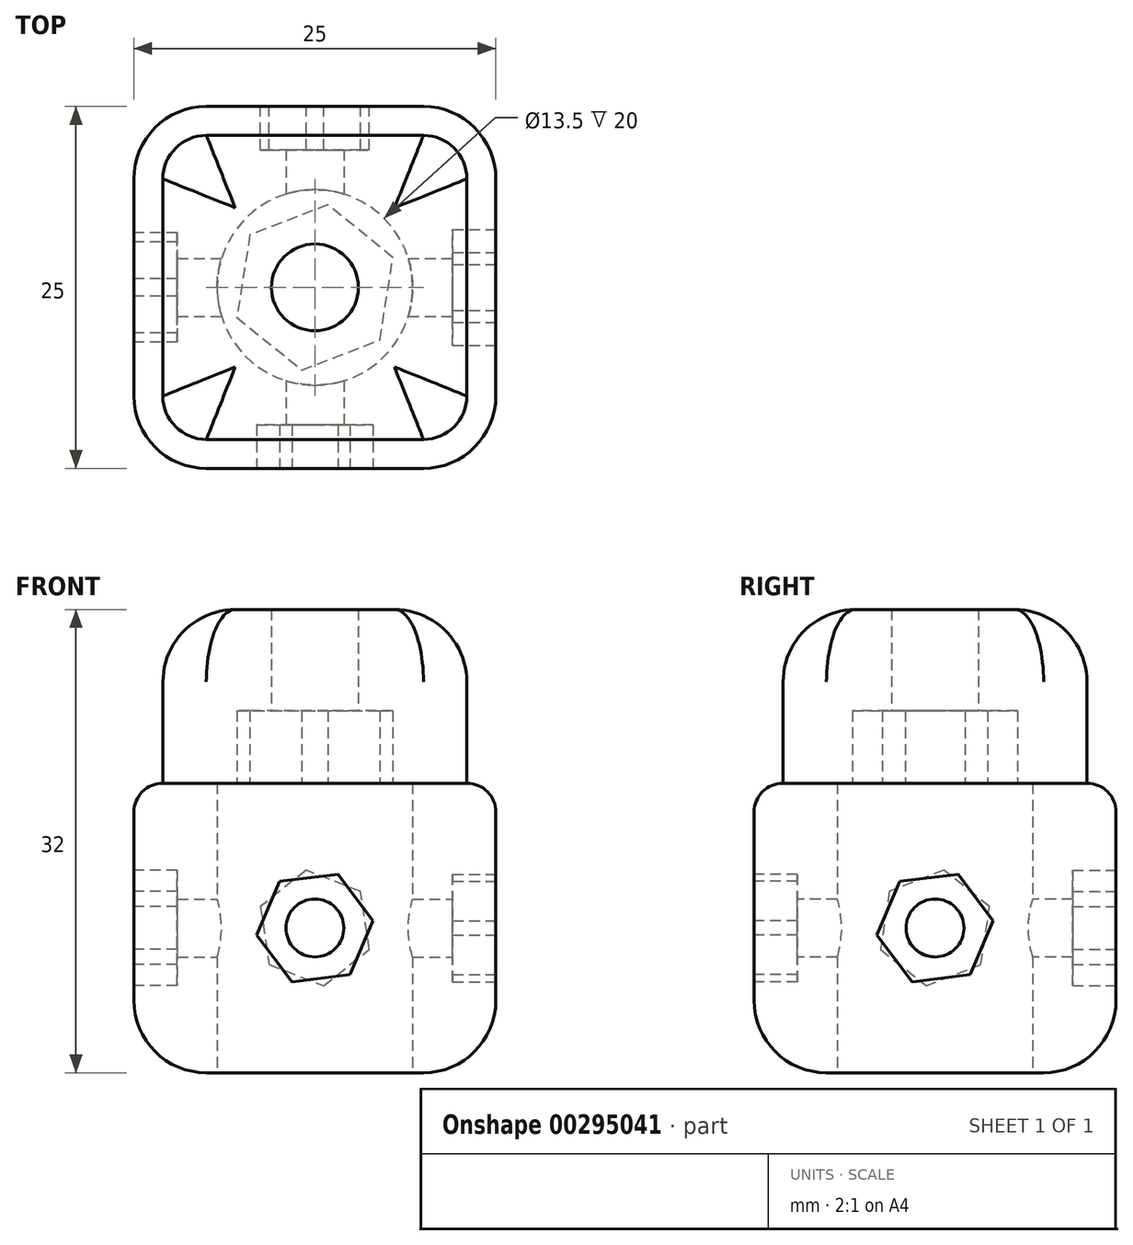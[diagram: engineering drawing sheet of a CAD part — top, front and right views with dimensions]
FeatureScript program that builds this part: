
annotation { "Feature Type Name" : "Feature", "Feature Type Description" : "" }
export const myFeature = defineFeature(function(context is Context, id is Id, definition is map)
    precondition{}
    {
        {
            var Q0;
            Q0=qCreatedBy(makeId("Top.planeOp"),FACE);
            var sketch = newSketch(context, id + "F0", { "sketchPlane" : qUnion([Q0])});
            skLineSegment(sketch, "E0.bottom", {"start": v(12.5, 12.5) * mm, "end": v(-12.5, 12.5) * mm});
            skLineSegment(sketch, "E0.top", {"start": v(12.5, -12.5) * mm, "end": v(-12.5, -12.5) * mm});
            skLineSegment(sketch, "E0.left", {"start": v(12.5, 12.5) * mm, "end": v(12.5, -12.5) * mm});
            skLineSegment(sketch, "E0.right", {"start": v(-12.5, 12.5) * mm, "end": v(-12.5, -12.5) * mm});
            skPoint(sketch, "E0.middle", {"position": v(0, 0) * mm});
            skSolve(sketch);
        }
        {
            var Q0;
            Q0 = qSketchRegion(id + "F0", true);
            extrude(context, id + "F1", {"entities" : qUnion([Q0]), "depth" : 20 * mm});
        }
        {
            var Q0;
            Q0=makeQuery(id+"F1.opExtrude","CAP_FACE",FACE,{"disambiguationData":[OSD([sQuery(id+"F0.wireOp",EDGE,"E0.bottom"),sQuery(id+"F0.wireOp",EDGE,"E0.top"),sQuery(id+"F0.wireOp",EDGE,"E0.left"),sQuery(id+"F0.wireOp",EDGE,"E0.right")])],"isStart":false});
            var sketch = newSketch(context, id + "F2", { "sketchPlane" : qUnion([Q0])});
            skLineSegment(sketch, "E1.bottom", {"start": v(10.5, 10.5) * mm, "end": v(-10.5, 10.5) * mm});
            skLineSegment(sketch, "E1.top", {"start": v(10.5, -10.5) * mm, "end": v(-10.5, -10.5) * mm});
            skLineSegment(sketch, "E1.left", {"start": v(10.5, 10.5) * mm, "end": v(10.5, -10.5) * mm});
            skLineSegment(sketch, "E1.right", {"start": v(-10.5, 10.5) * mm, "end": v(-10.5, -10.5) * mm});
            skSolve(sketch);
        }
        {
            var Q0;
            Q0=makeQuery(id+"F2.imprint","IMPRINT",FACE,{"disambiguationData":[TD([[makeQuery(id+"F2.imprint","IMPRINT",EDGE,{"derivedFrom":sQuery(id+"F2.wireOp",EDGE,"E1.bottom")}),1.0]])]});
            extrude(context, id + "F3", {"entities" : qUnion([Q0]), "operationType" : NewBodyOperationType.ADD, "depth" : 12 * mm});
        }
        {
            var Q0;
            Q0=makeQuery(id+"F1.opExtrude","CAP_FACE",FACE,{"disambiguationData":[OSD([sQuery(id+"F0.wireOp",EDGE,"E0.bottom"),sQuery(id+"F0.wireOp",EDGE,"E0.top"),sQuery(id+"F0.wireOp",EDGE,"E0.left"),sQuery(id+"F0.wireOp",EDGE,"E0.right")])],"isStart":true});
            var sketch = newSketch(context, id + "F4", { "sketchPlane" : qUnion([Q0])});
            skCircle(sketch, "E2", {"center": v(0, 0) * mm, "radius": 6.75 * mm});
            skSolve(sketch);
        }
        {
            var Q0;
            Q0=makeQuery(id+"F4.imprint","IMPRINT",FACE,{"disambiguationData":[TD([[makeQuery(id+"F4.imprint","IMPRINT",EDGE,{"derivedFrom":sQuery(id+"F4.wireOp",EDGE,"E2")}),1.0]])]});
            extrude(context, id + "F5", {"entities" : qUnion([Q0]), "operationType" : NewBodyOperationType.REMOVE, "oppositeDirection" : true, "depth" : 20 * mm});
        }
        {
            var Q0;
            Q0=makeQuery(id+"F1.opExtrude","CAP_FACE",FACE,{"disambiguationData":[OSD([sQuery(id+"F0.wireOp",EDGE,"E0.bottom"),sQuery(id+"F0.wireOp",EDGE,"E0.top"),sQuery(id+"F0.wireOp",EDGE,"E0.left"),sQuery(id+"F0.wireOp",EDGE,"E0.right")])],"isStart":true});
            var sketch = newSketch(context, id + "F6", { "sketchPlane" : qUnion([Q0])});
            skCircle(sketch, "E3", {"center": v(0, 0) * mm, "radius": 3 * mm});
            skSolve(sketch);
        }
        {
            var Q0;
            Q0 = qSketchRegion(id + "F6", true);
            extrude(context, id + "F7", {"entities" : qUnion([Q0]), "operationType" : NewBodyOperationType.REMOVE, "endBound" : BoundingType.THROUGH_ALL, "oppositeDirection" : true, "depth" : 25 * mm});
        }
        {
            var Q0;
            Q0=makeQuery(id+"F1.opExtrude","SWEPT_FACE",FACE,{"disambiguationData":[OSD([sQuery(id+"F0.wireOp",EDGE,"E0.right")])]});
            var sketch = newSketch(context, id + "F8", { "sketchPlane" : qUnion([Q0])});
            skLineSegment(sketch, "E4", {"start": v(-12.5, 0) * mm, "end": v(12.5, 20) * mm, "construction": true});
            skPoint(sketch, "E5.0.midPoint", {"position": v(1.27, 7.28) * mm});
            skCircle(sketch, "E6.cCircle", {"center": v(0, 10) * mm, "radius": 3.5 * mm, "construction": true});
            skLineSegment(sketch, "E6.0", {"start": v(3.76, 8.53) * mm, "end": v(0.6, 6) * mm});
            skLineSegment(sketch, "E6.1", {"start": v(0.6, 6) * mm, "end": v(-3.16, 7.48) * mm});
            skLineSegment(sketch, "E6.2", {"start": v(-3.16, 7.48) * mm, "end": v(-3.76, 11.47) * mm});
            skLineSegment(sketch, "E6.3", {"start": v(-3.76, 11.47) * mm, "end": v(-0.6, 14) * mm});
            skLineSegment(sketch, "E6.4", {"start": v(-0.6, 14) * mm, "end": v(3.16, 12.52) * mm});
            skLineSegment(sketch, "E6.5", {"start": v(3.16, 12.52) * mm, "end": v(3.76, 8.53) * mm});
            skPoint(sketch, "E6.0.midPoint", {"position": v(2.19, 7.27) * mm});
            skSolve(sketch);
        }
        {
            var Q0;
            Q0 = qSketchRegion(id + "F8", true);
            extrude(context, id + "F9", {"entities" : qUnion([Q0]), "operationType" : NewBodyOperationType.REMOVE, "oppositeDirection" : true, "depth" : 3 * mm});
        }
        {
            var Q0;
            Q0=makeQuery(id+"F1.opExtrude","SWEPT_FACE",FACE,{"disambiguationData":[OSD([sQuery(id+"F0.wireOp",EDGE,"E0.bottom")])]});
            var sketch = newSketch(context, id + "F10", { "sketchPlane" : qUnion([Q0])});
            skLineSegment(sketch, "E7", {"start": v(-12.5, 20) * mm, "end": v(12.5, 0) * mm, "construction": true});
            skCircle(sketch, "E8.cCircle", {"center": v(0, 10) * mm, "radius": 3.5 * mm, "construction": true});
            skLineSegment(sketch, "E8.0", {"start": v(-0.6, 6) * mm, "end": v(-3.76, 8.53) * mm});
            skLineSegment(sketch, "E8.1", {"start": v(-3.76, 8.53) * mm, "end": v(-3.16, 12.52) * mm});
            skLineSegment(sketch, "E8.2", {"start": v(-3.16, 12.52) * mm, "end": v(0.6, 14) * mm});
            skLineSegment(sketch, "E8.3", {"start": v(0.6, 14) * mm, "end": v(3.76, 11.47) * mm});
            skLineSegment(sketch, "E8.4", {"start": v(3.76, 11.47) * mm, "end": v(3.16, 7.48) * mm});
            skLineSegment(sketch, "E8.5", {"start": v(3.16, 7.48) * mm, "end": v(-0.6, 6) * mm});
            skPoint(sketch, "E8.0.midPoint", {"position": v(-2.19, 7.27) * mm});
            skSolve(sketch);
        }
        {
            var Q0;
            Q0=makeQuery(id+"F1.opExtrude","SWEPT_EDGE",EDGE,{"disambiguationData":[OSD([sQuery(id+"F0.wireOp",EDGE,"E0.bottom"),sQuery(id+"F0.wireOp",EDGE,"E0.left")])]});
            var Q1;
            Q1=makeQuery(id+"F1.opExtrude","SWEPT_EDGE",EDGE,{"disambiguationData":[OSD([sQuery(id+"F0.wireOp",EDGE,"E0.bottom"),sQuery(id+"F0.wireOp",EDGE,"E0.right")])]});
            var Q2;
            Q2=makeQuery(id+"F1.opExtrude","SWEPT_EDGE",EDGE,{"disambiguationData":[OSD([sQuery(id+"F0.wireOp",EDGE,"E0.top"),sQuery(id+"F0.wireOp",EDGE,"E0.left")])]});
            var Q3;
            Q3=makeQuery(id+"F1.opExtrude","SWEPT_EDGE",EDGE,{"disambiguationData":[OSD([sQuery(id+"F0.wireOp",EDGE,"E0.top"),sQuery(id+"F0.wireOp",EDGE,"E0.right")])]});
            fillet(context, id + "F11", {"entities" : qUnion([Q0, Q1, Q2, Q3]), "radius" : 5 * mm, "tangentPropagation" : true, "allowEdgeOverflow" : false});
        }
        {
            var Q0;
            Q0=makeQuery(id+"F3.opExtrude","SWEPT_EDGE",EDGE,{"disambiguationData":[OSD([sQuery(id+"F2.wireOp",EDGE,"E1.bottom"),sQuery(id+"F2.wireOp",EDGE,"E1.right")])]});
            var Q1;
            Q1=makeQuery(id+"F3.opExtrude","SWEPT_EDGE",EDGE,{"disambiguationData":[OSD([sQuery(id+"F2.wireOp",EDGE,"E1.top"),sQuery(id+"F2.wireOp",EDGE,"E1.right")])]});
            var Q2;
            Q2=makeQuery(id+"F3.opExtrude","SWEPT_EDGE",EDGE,{"disambiguationData":[OSD([sQuery(id+"F2.wireOp",EDGE,"E1.top"),sQuery(id+"F2.wireOp",EDGE,"E1.left")])]});
            var Q3;
            Q3=makeQuery(id+"F3.opExtrude","SWEPT_EDGE",EDGE,{"disambiguationData":[OSD([sQuery(id+"F2.wireOp",EDGE,"E1.bottom"),sQuery(id+"F2.wireOp",EDGE,"E1.left")])]});
            fillet(context, id + "F12", {"entities" : qUnion([Q0, Q1, Q2, Q3]), "radius" : 3 * mm, "tangentPropagation" : true, "allowEdgeOverflow" : false});
        }
        {
            var Q0;
            Q0 = qSketchRegion(id + "F10", true);
            extrude(context, id + "F13", {"entities" : qUnion([Q0]), "operationType" : NewBodyOperationType.REMOVE, "oppositeDirection" : true, "depth" : 3 * mm});
        }
        {
            var Q0;
            Q0=makeQuery(id+"F1.opExtrude","SWEPT_FACE",FACE,{"disambiguationData":[OSD([sQuery(id+"F0.wireOp",EDGE,"E0.left")])]});
            var sketch = newSketch(context, id + "F14", { "sketchPlane" : qUnion([Q0])});
            skLineSegment(sketch, "E9", {"start": v(7.5, 0) * mm, "end": v(-7.5, 20) * mm, "construction": true});
            skCircle(sketch, "E10.cCircle", {"center": v(0, 10) * mm, "radius": 3.5 * mm, "construction": true});
            skLineSegment(sketch, "E10.0", {"start": v(-1.59, 6.28) * mm, "end": v(-4.01, 9.52) * mm});
            skLineSegment(sketch, "E10.1", {"start": v(-4.01, 9.52) * mm, "end": v(-2.42, 13.23) * mm});
            skLineSegment(sketch, "E10.2", {"start": v(-2.42, 13.23) * mm, "end": v(1.59, 13.72) * mm});
            skLineSegment(sketch, "E10.3", {"start": v(1.59, 13.72) * mm, "end": v(4.01, 10.48) * mm});
            skLineSegment(sketch, "E10.4", {"start": v(4.01, 10.48) * mm, "end": v(2.42, 6.77) * mm});
            skLineSegment(sketch, "E10.5", {"start": v(2.42, 6.77) * mm, "end": v(-1.59, 6.28) * mm});
            skPoint(sketch, "E10.0.midPoint", {"position": v(-2.8, 7.9) * mm});
            skSolve(sketch);
        }
        {
            var Q0;
            Q0 = qSketchRegion(id + "F14", true);
            extrude(context, id + "F15", {"entities" : qUnion([Q0]), "operationType" : NewBodyOperationType.REMOVE, "oppositeDirection" : true, "depth" : 3 * mm});
        }
        {
            var Q0;
            Q0=makeQuery(id+"F1.opExtrude","SWEPT_FACE",FACE,{"disambiguationData":[OSD([sQuery(id+"F0.wireOp",EDGE,"E0.top")])]});
            var sketch = newSketch(context, id + "F16", { "sketchPlane" : qUnion([Q0])});
            skLineSegment(sketch, "E11", {"start": v(7.5, 0) * mm, "end": v(-7.5, 20) * mm, "construction": true});
            skCircle(sketch, "E12.cCircle", {"center": v(0, 10) * mm, "radius": 3.5 * mm, "construction": true});
            skLineSegment(sketch, "E12.0", {"start": v(-1.59, 6.28) * mm, "end": v(-4.01, 9.52) * mm});
            skLineSegment(sketch, "E12.1", {"start": v(-4.01, 9.52) * mm, "end": v(-2.42, 13.23) * mm});
            skLineSegment(sketch, "E12.2", {"start": v(-2.42, 13.23) * mm, "end": v(1.59, 13.72) * mm});
            skLineSegment(sketch, "E12.3", {"start": v(1.59, 13.72) * mm, "end": v(4.01, 10.48) * mm});
            skLineSegment(sketch, "E12.4", {"start": v(4.01, 10.48) * mm, "end": v(2.42, 6.77) * mm});
            skLineSegment(sketch, "E12.5", {"start": v(2.42, 6.77) * mm, "end": v(-1.59, 6.28) * mm});
            skPoint(sketch, "E12.0.midPoint", {"position": v(-2.8, 7.9) * mm});
            skSolve(sketch);
        }
        {
            var Q0;
            Q0 = qSketchRegion(id + "F16", true);
            extrude(context, id + "F17", {"entities" : qUnion([Q0]), "operationType" : NewBodyOperationType.REMOVE, "oppositeDirection" : true, "depth" : 3 * mm});
        }
        {
            var Q0;
            Q0=makeQuery(id+"F17.boolean.opBoolean","COPY",FACE,{"derivedFrom":makeQuery(id+"F17.opExtrude","CAP_FACE",FACE,{"disambiguationData":[OSD([sQuery(id+"F16.wireOp",EDGE,"E12.0"),sQuery(id+"F16.wireOp",EDGE,"E12.1"),sQuery(id+"F16.wireOp",EDGE,"E12.2"),sQuery(id+"F16.wireOp",EDGE,"E12.3"),sQuery(id+"F16.wireOp",EDGE,"E12.4"),sQuery(id+"F16.wireOp",EDGE,"E12.5")])],"isStart":false})});
            var sketch = newSketch(context, id + "F18", { "sketchPlane" : qUnion([Q0])});
            skLineSegment(sketch, "E13", {"start": v(4.01, 10.48) * mm, "end": v(-4.01, 9.52) * mm, "construction": true});
            skCircle(sketch, "E14", {"center": v(0, 10) * mm, "radius": 2 * mm});
            skSolve(sketch);
        }
        {
            var Q0;
            Q0 = qSketchRegion(id + "F18", true);
            extrude(context, id + "F19", {"entities" : qUnion([Q0]), "operationType" : NewBodyOperationType.REMOVE, "endBound" : BoundingType.THROUGH_ALL, "oppositeDirection" : true, "depth" : 25 * mm});
        }
        {
            var Q0;
            Q0=makeQuery(id+"F15.boolean.opBoolean","COPY",FACE,{"derivedFrom":makeQuery(id+"F15.opExtrude","CAP_FACE",FACE,{"disambiguationData":[OSD([sQuery(id+"F14.wireOp",EDGE,"E10.0"),sQuery(id+"F14.wireOp",EDGE,"E10.1"),sQuery(id+"F14.wireOp",EDGE,"E10.2"),sQuery(id+"F14.wireOp",EDGE,"E10.3"),sQuery(id+"F14.wireOp",EDGE,"E10.4"),sQuery(id+"F14.wireOp",EDGE,"E10.5")])],"isStart":false})});
            var sketch = newSketch(context, id + "F20", { "sketchPlane" : qUnion([Q0])});
            skLineSegment(sketch, "E15", {"start": v(-1.59, 6.28) * mm, "end": v(1.59, 13.72) * mm, "construction": true});
            skCircle(sketch, "E16", {"center": v(0, 10) * mm, "radius": 2 * mm});
            skSolve(sketch);
        }
        {
            var Q0;
            Q0 = qSketchRegion(id + "F20", true);
            extrude(context, id + "F21", {"entities" : qUnion([Q0]), "operationType" : NewBodyOperationType.REMOVE, "endBound" : BoundingType.THROUGH_ALL, "oppositeDirection" : true, "depth" : 25 * mm});
        }
        {
            var Q0;
            {var subQ0=sQuery(id+"F0.wireOp",EDGE,"E0.right");var subQ1=sQuery(id+"F0.wireOp",EDGE,"E0.bottom");Q0=makeQuery(id+"F11.opFillet","BLEND_EDGE",EDGE,{"blendedFrom":[makeQuery(id+"F1.opExtrude","SWEPT_EDGE",EDGE,{"disambiguationData":[OSD([subQ1,subQ0])]}),makeQuery(id+"F1.opExtrude","CAP_FACE",FACE,{"disambiguationData":[OSD([subQ1,sQuery(id+"F0.wireOp",EDGE,"E0.top"),sQuery(id+"F0.wireOp",EDGE,"E0.left"),subQ0])],"isStart":true})],"blendedInto":[makeQuery(id+"F1.opExtrude","CAP_FACE",FACE,{"disambiguationData":[OSD([subQ1,sQuery(id+"F0.wireOp",EDGE,"E0.top"),sQuery(id+"F0.wireOp",EDGE,"E0.left"),subQ0])],"isStart":true})]});}
            fillet(context, id + "F22", {"entities" : qUnion([Q0]), "radius" : 5 * mm, "tangentPropagation" : true, "allowEdgeOverflow" : false});
        }
        {
            var Q0;
            {var subQ0=sQuery(id+"F0.wireOp",EDGE,"E0.right");var subQ1=sQuery(id+"F0.wireOp",EDGE,"E0.top");Q0=makeQuery(id+"F11.opFillet","BLEND_EDGE",EDGE,{"blendedFrom":[makeQuery(id+"F1.opExtrude","SWEPT_EDGE",EDGE,{"disambiguationData":[OSD([subQ1,subQ0])]}),makeQuery(id+"F1.opExtrude","CAP_FACE",FACE,{"disambiguationData":[OSD([sQuery(id+"F0.wireOp",EDGE,"E0.bottom"),subQ1,sQuery(id+"F0.wireOp",EDGE,"E0.left"),subQ0])],"isStart":false})],"blendedInto":[makeQuery(id+"F1.opExtrude","CAP_FACE",FACE,{"disambiguationData":[OSD([sQuery(id+"F0.wireOp",EDGE,"E0.bottom"),subQ1,sQuery(id+"F0.wireOp",EDGE,"E0.left"),subQ0])],"isStart":false})]});}
            fillet(context, id + "F23", {"entities" : qUnion([Q0]), "radius" : 2 * mm, "tangentPropagation" : true, "allowEdgeOverflow" : false});
        }
        {
            var Q0;
            Q0=makeQuery(id+"F1.opExtrude","CAP_FACE",FACE,{"disambiguationData":[OSD([sQuery(id+"F0.wireOp",EDGE,"E0.bottom"),sQuery(id+"F0.wireOp",EDGE,"E0.top"),sQuery(id+"F0.wireOp",EDGE,"E0.left"),sQuery(id+"F0.wireOp",EDGE,"E0.right")])],"isStart":true});
            var sketch = newSketch(context, id + "F24", { "sketchPlane" : qUnion([Q0])});
            skCircle(sketch, "E17.cCircle", {"center": v(0, 0) * mm, "radius": 5 * mm, "construction": true});
            skLineSegment(sketch, "E17.0", {"start": v(-0.9, 5.7) * mm, "end": v(4.48, 3.64) * mm});
            skLineSegment(sketch, "E17.1", {"start": v(4.48, 3.64) * mm, "end": v(5.4, -2.06) * mm});
            skLineSegment(sketch, "E17.2", {"start": v(5.4, -2.06) * mm, "end": v(0.9, -5.7) * mm});
            skLineSegment(sketch, "E17.3", {"start": v(0.9, -5.7) * mm, "end": v(-4.48, -3.64) * mm});
            skLineSegment(sketch, "E17.4", {"start": v(-4.48, -3.64) * mm, "end": v(-5.4, 2.06) * mm});
            skLineSegment(sketch, "E17.5", {"start": v(-5.4, 2.06) * mm, "end": v(-0.9, 5.7) * mm});
            skPoint(sketch, "E17.0.midPoint", {"position": v(1.79, 4.67) * mm});
            skSolve(sketch);
        }
        {
            var Q0;
            Q0=makeQuery(id+"F24.imprint","IMPRINT",FACE,{"disambiguationData":[TD([[makeQuery(id+"F24.imprint","IMPRINT",EDGE,{"derivedFrom":sQuery(id+"F24.wireOp",EDGE,"E17.0")}),-1.0]])]});
            extrude(context, id + "F25", {"entities" : qUnion([Q0]), "operationType" : NewBodyOperationType.REMOVE, "oppositeDirection" : true, "depth" : 25 * mm});
        }
        {
            var Q0;
            {var subQ0=sQuery(id+"F2.wireOp",EDGE,"E1.right");var subQ1=sQuery(id+"F2.wireOp",EDGE,"E1.top");Q0=makeQuery(id+"F12.opFillet","BLEND_EDGE",EDGE,{"blendedFrom":[makeQuery(id+"F3.opExtrude","SWEPT_EDGE",EDGE,{"disambiguationData":[OSD([subQ1,subQ0])]}),makeQuery(id+"F3.opExtrude","CAP_FACE",FACE,{"disambiguationData":[OSD([sQuery(id+"F2.wireOp",EDGE,"E1.bottom"),subQ1,sQuery(id+"F2.wireOp",EDGE,"E1.left"),subQ0])],"isStart":false})],"blendedInto":[makeQuery(id+"F3.opExtrude","CAP_FACE",FACE,{"disambiguationData":[OSD([sQuery(id+"F2.wireOp",EDGE,"E1.bottom"),subQ1,sQuery(id+"F2.wireOp",EDGE,"E1.left"),subQ0])],"isStart":false})]});}
            fillet(context, id + "F26", {"entities" : qUnion([Q0]), "radius" : 5 * mm, "tangentPropagation" : true, "allowEdgeOverflow" : false});
        }
    });
